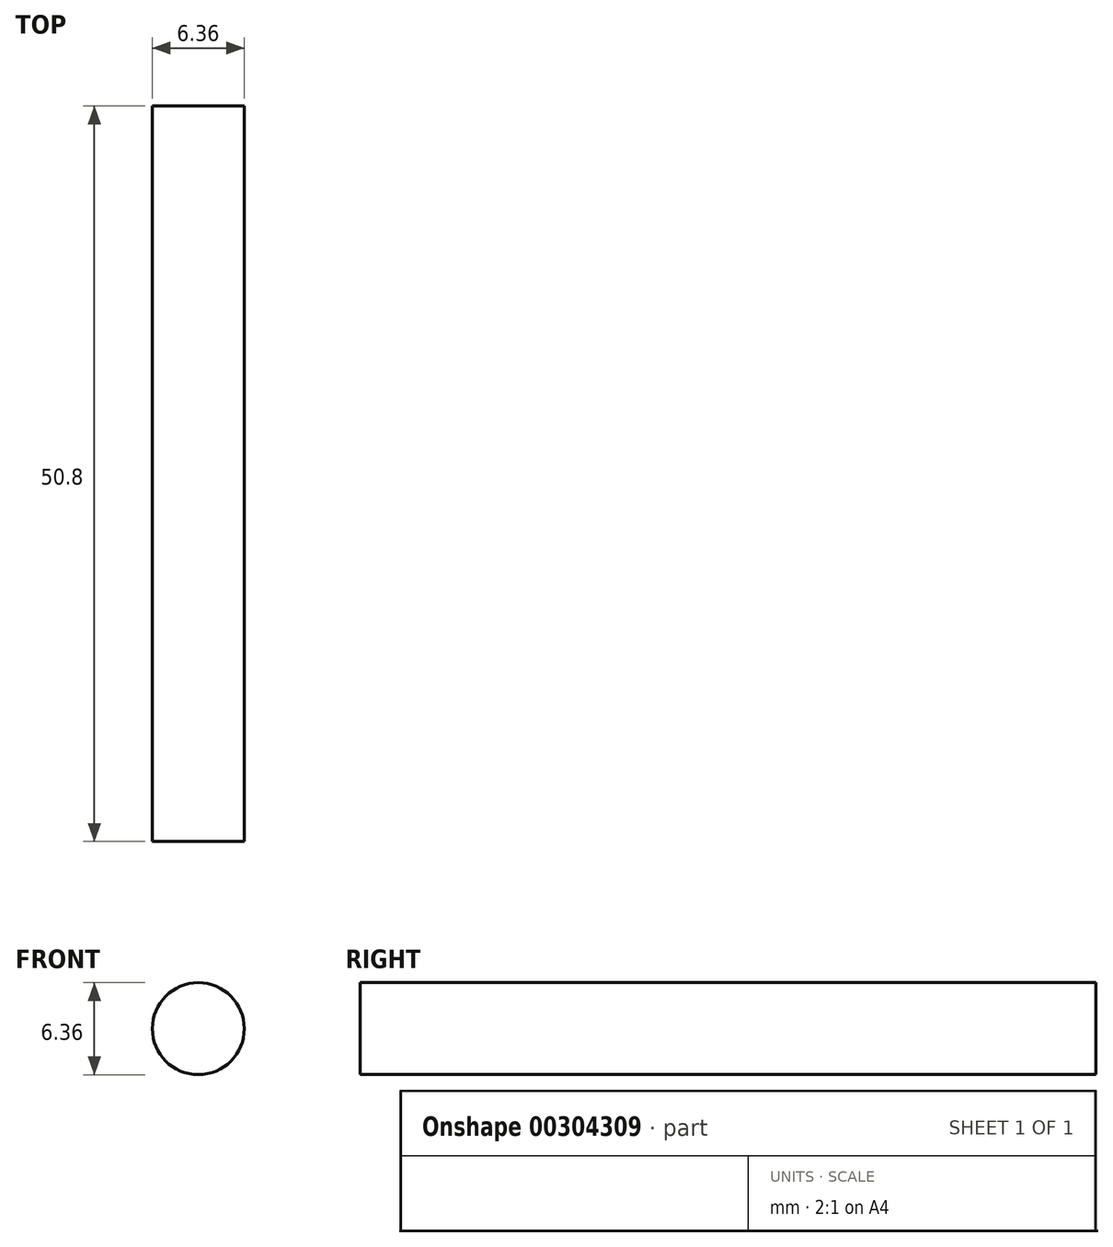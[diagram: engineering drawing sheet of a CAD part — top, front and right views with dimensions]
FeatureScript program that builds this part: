
annotation { "Feature Type Name" : "Feature", "Feature Type Description" : "" }
export const myFeature = defineFeature(function(context is Context, id is Id, definition is map)
    precondition{}
    {
        {
            var Q0;
            Q0=qCreatedBy(makeId("Front.planeOp"),FACE);
            var sketch = newSketch(context, id + "F0", { "sketchPlane" : qUnion([Q0])});
            skCircle(sketch, "E0", {"center": v(0, 0) * mm, "radius": 3.18 * mm});
            skSolve(sketch);
        }
        {
            var Q0;
            Q0 = qSketchRegion(id + "F0", true);
            extrude(context, id + "F1", {"entities" : qUnion([Q0]), "oppositeDirection" : true, "depth" : 50.8 * mm});
        }
    });
